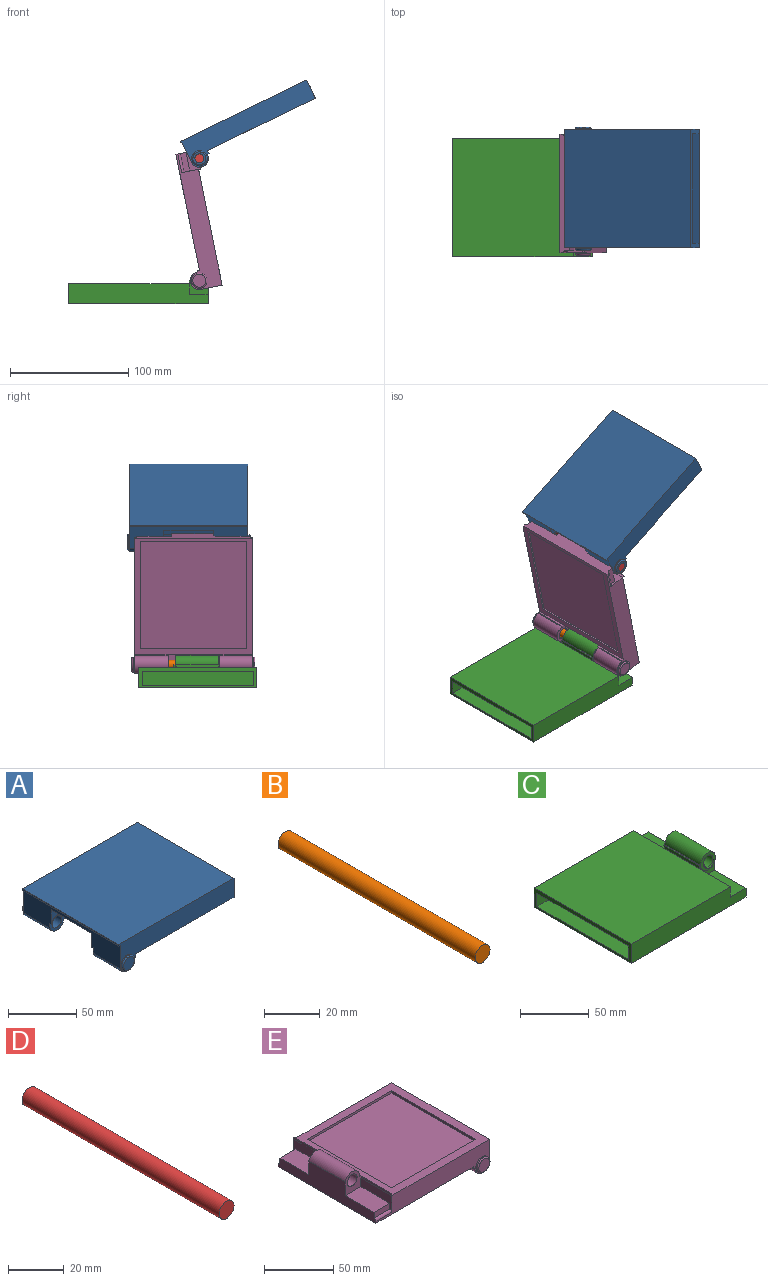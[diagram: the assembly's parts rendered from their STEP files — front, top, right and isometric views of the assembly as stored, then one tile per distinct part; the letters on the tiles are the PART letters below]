
ASSEMBLY  parts=5 mates=4
PART A: 39 faces, bbox 119x104x27.5 mm
  f0: cylinder r=7.5mm len=27.5mm, axis (0,1,0), area 589.4mm2, adj f5,f9,f14,f36
  f1: cylinder r=7.5mm len=14.7mm, axis (0,1,0), area 32.2mm2, adj f5,f7,f9,f36
  f2: cylinder r=7.5mm len=27.5mm, axis (0,1,0), area 589.4mm2, adj f6,f9,f10,f36
  f3: plane 42x15.7mm, normal (0,0,-1), area 659.4mm2, adj f7,f8,f15,f36
  f4: cylinder r=7.5mm len=14.7mm, axis (0,1,0), area 32.2mm2, adj f6,f8,f9,f36
  f5: plane 15x14.7mm, normal (0,1,0), area 97.3mm2, adj f0,f1,f23,f36
  f6: plane 15x14.7mm, normal (0,-1,0), area 97.3mm2, adj f2,f4,f25,f36
  f7: plane 15.7x15mm, normal (0,1,0), area 147.6mm2, adj f1,f3,f9,f15,f36
  f8: plane 15.7x15mm, normal (0,-1,0), area 147.6mm2, adj f3,f4,f9,f15,f36
  f9: plane 100x1.55mm, normal (0,0,-1), area 113mm2, adj f0,f1,f2,f4,f7,f8,f10,f14
  f10: plane 119x27.5mm, normal (0,1,0), area 2009.2mm2, adj f2,f9,f12,f13,f17,f34,f35,f36
  f11: plane 100x92.5mm, normal (0,0,1), area 1768mm2, adj f12,f27,f28,f29,f30,f31,f32,f33
  f12: plane 100x17.03mm, normal (1,0,0), area 500.3mm2, adj f10,f11,f13,f14,f26,f27,f28,f35
  f13: plane 119x100mm, normal (0,0,1), area 11900mm2, adj f10,f12,f14,f38
  f14: plane 119x27.5mm, normal (0,-1,0), area 2009.2mm2, adj f0,f9,f12,f13,f18,f34,f35,f36
  f15: plane 42x15mm, normal (-1,0,0), area 630mm2, adj f3,f7,f8,f9
  f16: plane 11x11mm, normal (0,1,0), area 95mm2, adj f21
  f17: cylinder r=6.5mm len=13mm, axis (0,-1,0), area 40.8mm2, adj f10,f21
  f18: cylinder r=6.5mm len=13mm, axis (0,1,0), area 40.8mm2, adj f14,f20
  f19: plane 11x11mm, normal (0,-1,0), area 95mm2, adj f20
  f20: torus R=5.5mm, axis (0,-1,0), area 60.6mm2, adj f18,f19
  f21: torus R=5.5mm, axis (0,1,0), area 60.6mm2, adj f16,f17
  f22: plane 10x10mm, normal (0,1,0), area 78.5mm2, adj f23
  f23: cylinder r=5mm len=25.5mm, axis (0,1,0), area 801.1mm2, adj f5,f22
  f24: plane 10x10mm, normal (0,-1,0), area 78.5mm2, adj f25
  f25: cylinder r=5mm len=25.5mm, axis (0,1,0), area 801.1mm2, adj f6,f24
  f26: plane 100x92.5mm, normal (0,0,-1), area 9250mm2, adj f12,f27,f28,f29
  f27: plane 100x13mm, normal (0,1,0), area 1300mm2, adj f11,f12,f26,f29
  f28: plane 100x13mm, normal (0,-1,0), area 1300mm2, adj f11,f12,f26,f29
  f29: plane 92.5x13mm, normal (1,0,0), area 1202.5mm2, adj f11,f26,f27,f28
  f30: plane 86x0.5mm, normal (0,1,0), area 43mm2, adj f11,f31,f33,f35
  f31: plane 87x0.5mm, normal (1,0,0), area 43.5mm2, adj f11,f30,f32,f35
  f32: plane 86x0.5mm, normal (0,-1,0), area 43mm2, adj f11,f31,f33,f35
  f33: plane 87x0.5mm, normal (-1,0,0), area 43.5mm2, adj f11,f30,f32,f35
  f34: plane 100x2.97mm, normal (1,0,0), area 297.2mm2, adj f9,f10,f14,f35
  f35: plane 101.45x100mm, normal (0,0,-1), area 2663mm2, adj f10,f12,f14,f30,f31,f32,f33,f34
  f36: plane 100x20.94mm, normal (-1,0,0), area 1363mm2, adj f0,f1,f2,f3,f4,f5,f6,f7
  f37: plane 100x1.3mm, normal (0,0,-1), area 130mm2, adj f10,f14,f36,f38
  f38: plane 100x1.16mm, normal (-1,0,0), area 116.2mm2, adj f10,f13,f14,f37
PART B: 3 faces, bbox 7.5x100x7.5 mm
  f0: cylinder r=3.75mm len=100mm, axis (0,1,0), area 2356.2mm2, adj f1,f2
  f1: plane 7.5x7.5mm, normal (0,-1,0), area 44.2mm2, adj f0
  f2: plane 7.5x7.5mm, normal (0,1,0), area 44.2mm2, adj f0
PART C: 31 faces, bbox 118x100x27.5 mm
  f0: plane 118x100mm, normal (0,0,-1), area 11800mm2, adj f7,f10,f11,f30
  f1: plane 32x16mm, normal (0,0,1), area 512mm2, adj f5,f11,f12,f30
  f2: plane 32x16mm, normal (0,0,1), area 512mm2, adj f6,f10,f13,f30
  f3: plane 16x15.3mm, normal (0,-1,0), area 100mm2, adj f8,f9,f14,f16,f21,f22,f29,f30
  f4: plane 16x15.3mm, normal (0,1,0), area 100mm2, adj f8,f9,f15,f16,f19,f20,f29,f30
  f5: plane 16x11.7mm, normal (0,1,0), area 98.8mm2, adj f1,f12,f19,f20,f29,f30
  f6: plane 16x11.7mm, normal (0,-1,0), area 98.8mm2, adj f2,f13,f21,f22,f29,f30
  f7: plane 100x17.17mm, normal (-1,0,0), area 589.2mm2, adj f0,f10,f11,f23,f24,f25,f26,f28
  f8: plane 37x1mm, normal (0,0,1), area 37mm2, adj f3,f4,f9,f29
  f9: cylinder r=7.5mm len=37mm, axis (0,-1,0), area 871.8mm2, adj f3,f4,f8,f30
  f10: plane 118x17.17mm, normal (0,-1,0), area 1879.6mm2, adj f0,f2,f7,f13,f28,f30
  f11: plane 118x17.17mm, normal (0,1,0), area 1879.6mm2, adj f0,f1,f7,f12,f28,f30
  f12: plane 32x9.17mm, normal (1,0,0), area 293.5mm2, adj f1,f5,f11,f28
  f13: plane 32x9.17mm, normal (1,0,0), area 293.5mm2, adj f2,f6,f10,f28
  f14: cylinder r=5mm len=10mm, axis (0,1,0), area 24mm2, adj f3,f16,f17
  f15: cylinder r=5mm len=10mm, axis (0,1,0), area 24mm2, adj f4,f16,f18
  f16: cylinder r=5mm len=40mm, axis (0,1,0), area 1208.6mm2, adj f3,f4,f14,f15,f17,f18
  f17: plane 10x5.15mm, normal (0,-1,0), area 3mm2, adj f14,f16
  f18: plane 10x5.15mm, normal (0,1,0), area 3mm2, adj f15,f16
  f19: plane 1x0.5mm, normal (0,0,-1), area 0.5mm2, adj f4,f5,f20,f29
  f20: cylinder r=7.5mm len=15mm, axis (0,1,0), area 11.8mm2, adj f4,f5,f19,f30
  f21: plane 1x0.5mm, normal (0,0,-1), area 0.5mm2, adj f3,f6,f22,f29
  f22: cylinder r=7.5mm len=15mm, axis (0,1,0), area 11.8mm2, adj f3,f6,f21,f30
  f23: plane 94x92.5mm, normal (0,0,-1), area 8695mm2, adj f7,f24,f26,f27
  f24: plane 92.5x12mm, normal (0,-1,0), area 1110mm2, adj f7,f23,f25,f27
  f25: plane 94x92.5mm, normal (0,0,1), area 8695mm2, adj f7,f24,f26,f27
  f26: plane 92.5x12mm, normal (0,1,0), area 1110mm2, adj f7,f23,f25,f27
  f27: plane 94x12mm, normal (-1,0,0), area 1128mm2, adj f23,f24,f25,f26
  f28: plane 102x100mm, normal (0,0,1), area 10200mm2, adj f7,f10,f11,f12,f13,f29
  f29: plane 37x2.83mm, normal (-1,0,0), area 102.1mm2, adj f3,f4,f5,f6,f8,f19,f21,f28
  f30: plane 100x20mm, normal (1,0,0), area 1232.3mm2, adj f0,f1,f2,f3,f4,f5,f6,f9
PART D: 3 faces, bbox 7.5x100x7.5 mm
  f0: cylinder r=3.75mm len=100mm, axis (0,1,0), area 2356.2mm2, adj f1,f2
  f1: plane 7.5x7.5mm, normal (0,-1,0), area 44.2mm2, adj f0
  f2: plane 7.5x7.5mm, normal (0,1,0), area 44.2mm2, adj f0
PART E: 50 faces, bbox 116x104x35.7 mm
  f0: plane 100x99.75mm, normal (0,0,1), area 2586.4mm2, adj f1,f2,f34,f44,f45,f46,f47,f48
  f1: plane 116x27.5mm, normal (0,-1,0), area 1637.3mm2, adj f0,f4,f14,f15,f17,f20,f23,f34
  f2: plane 116x27.5mm, normal (0,1,0), area 1637.3mm2, adj f0,f5,f12,f13,f15,f16,f22,f34
  f3: cylinder r=7.5mm len=37mm, axis (0,-1,0), area 819mm2, adj f6,f7,f15,f43
  f4: cylinder r=2mm len=16.09mm, axis (1,0,0), area 50.5mm2, adj f1,f8,f20,f43
  f5: cylinder r=2mm len=16.09mm, axis (-1,0,0), area 50.5mm2, adj f2,f10,f12,f43
  f6: plane 17.6x16.09mm, normal (0,1,0), area 170.9mm2, adj f3,f11,f12,f15,f33,f43
  f7: plane 17.6x16.09mm, normal (0,-1,0), area 170.9mm2, adj f3,f9,f15,f20,f33,f43
  f8: plane 16.09x5mm, normal (0,-1,0), area 80.4mm2, adj f4,f9,f20,f43
  f9: plane 29.5x16.09mm, normal (0,0,1), area 474.5mm2, adj f7,f8,f20,f43
  f10: plane 16.09x5mm, normal (0,1,0), area 80.4mm2, adj f5,f11,f12,f43
  f11: plane 29.5x16.09mm, normal (0,0,1), area 474.5mm2, adj f6,f10,f12,f43
  f12: plane 31.5x16.4mm, normal (-1,0,0), area 307mm2, adj f2,f5,f6,f10,f11,f15
  f13: plane 28.5x1mm, normal (0,0,-1), area 28.5mm2, adj f2,f16,f27,f37
  f14: plane 28.5x1mm, normal (0,0,-1), area 28.5mm2, adj f1,f17,f28,f35
  f15: plane 100x1.58mm, normal (0,0,1), area 68.9mm2, adj f1,f2,f3,f6,f7,f12,f20,f34
  f16: cylinder r=7.5mm len=28.5mm, axis (0,1,0), area 671.5mm2, adj f2,f13,f27,f44
  f17: cylinder r=7.5mm len=28.5mm, axis (0,1,0), area 671.5mm2, adj f1,f14,f28,f44
  f18: plane 43x13.08mm, normal (1,0,0), area 562.3mm2, adj f19,f27,f28,f36
  f19: plane 43x16mm, normal (0,0,-1), area 688mm2, adj f18,f27,f28,f44
  f20: plane 31.5x16.4mm, normal (-1,0,0), area 307mm2, adj f1,f4,f7,f8,f9,f15
  f21: plane 11x11mm, normal (0,1,0), area 95mm2, adj f26
  f22: cylinder r=6.5mm len=13mm, axis (0,-1,0), area 40.8mm2, adj f2,f26
  f23: cylinder r=6.5mm len=13mm, axis (0,1,0), area 40.8mm2, adj f1,f25
  f24: plane 11x11mm, normal (0,-1,0), area 95mm2, adj f25
  f25: torus R=5.5mm, axis (0,-1,0), area 60.6mm2, adj f23,f24
  f26: torus R=5.5mm, axis (0,1,0), area 60.6mm2, adj f21,f22
  f27: plane 22.5x16mm, normal (0,-1,0), area 249.8mm2, adj f13,f16,f18,f19,f30,f37,f44
  f28: plane 22.5x16mm, normal (0,1,0), area 249.8mm2, adj f14,f17,f18,f19,f32,f35,f44
  f29: plane 10x10mm, normal (0,-1,0), area 78.5mm2, adj f30
  f30: cylinder r=5mm len=26.5mm, axis (0,1,0), area 832.5mm2, adj f27,f29
  f31: plane 10x10mm, normal (0,1,0), area 78.5mm2, adj f32
  f32: cylinder r=5mm len=26.5mm, axis (0,1,0), area 832.5mm2, adj f28,f31
  f33: cylinder r=5mm len=37mm, axis (0,-1,0), area 1162.4mm2, adj f6,f7
  f34: plane 100x1.83mm, normal (1,0,0), area 182.8mm2, adj f0,f1,f2,f15
  f35: plane 28.5x1.92mm, normal (-1,0,0), area 54.8mm2, adj f1,f14,f28,f36
  f36: plane 100x100mm, normal (0,0,-1), area 1720mm2, adj f1,f2,f18,f35,f37,f39,f40,f41
  f37: plane 28.5x1.92mm, normal (-1,0,0), area 54.8mm2, adj f2,f13,f27,f36
  f38: plane 92x90mm, normal (0,0,-1), area 8280mm2, adj f39,f40,f41,f42
  f39: plane 90x1.38mm, normal (-1,0,0), area 124mm2, adj f36,f38,f40,f42
  f40: plane 92x1.38mm, normal (0,-1,0), area 126.7mm2, adj f36,f38,f39,f41
  f41: plane 90x1.38mm, normal (1,0,0), area 124mm2, adj f36,f38,f40,f42
  f42: plane 92x1.38mm, normal (0,1,0), area 126.7mm2, adj f36,f38,f39,f41
  f43: plane 100x20.88mm, normal (-1,0,0), area 1297.4mm2, adj f1,f2,f3,f4,f5,f6,f7,f8
  f44: plane 100x18.17mm, normal (1,0,0), area 1172.2mm2, adj f0,f1,f2,f16,f17,f19,f27,f28
  f45: plane 85.91x2mm, normal (0,-1,0), area 171.8mm2, adj f0,f46,f48,f49
  f46: plane 86x2mm, normal (1,0,0), area 172mm2, adj f0,f45,f47,f49
  f47: plane 85.91x2mm, normal (0,1,0), area 171.8mm2, adj f0,f46,f48,f49
  f48: plane 86x2mm, normal (-1,0,0), area 172mm2, adj f0,f45,f47,f49
  f49: plane 86x85.91mm, normal (0,0,1), area 7388.6mm2, adj f45,f46,f47,f48
PLACE A rot(axis=(0,-1,0),25.9deg) t=(139.69,7.5,88.78)mm
PLACE B rot(axis=(0,1,0),131.9deg) t=(118.93,5.5,18.94)mm
PLACE C t=(34.48,0,-17.34)mm fixed
PLACE D rot(axis=(0,-1,0),160.9deg) t=(43.76,5.5,120.86)mm
PLACE E rot(axis=(0,1,0),78.5deg) t=(75.21,3.5,31.11)mm
MATE pin_slot D.f0 <-> A.f0  axis (0,-1,0) through (85.08,-94.5,84.95)mm
MATE pin_slot B.f0 <-> E.f16  axis (0,1,0) through (84.98,5.5,-18.44)mm
MATE revolute E.f16 <-> C.f22  axis (0,1,0) through (84.98,-68,-18.44)mm
MATE revolute E.f3 <-> A.f0  axis (0,-1,0) through (85.08,-65,84.95)mm
